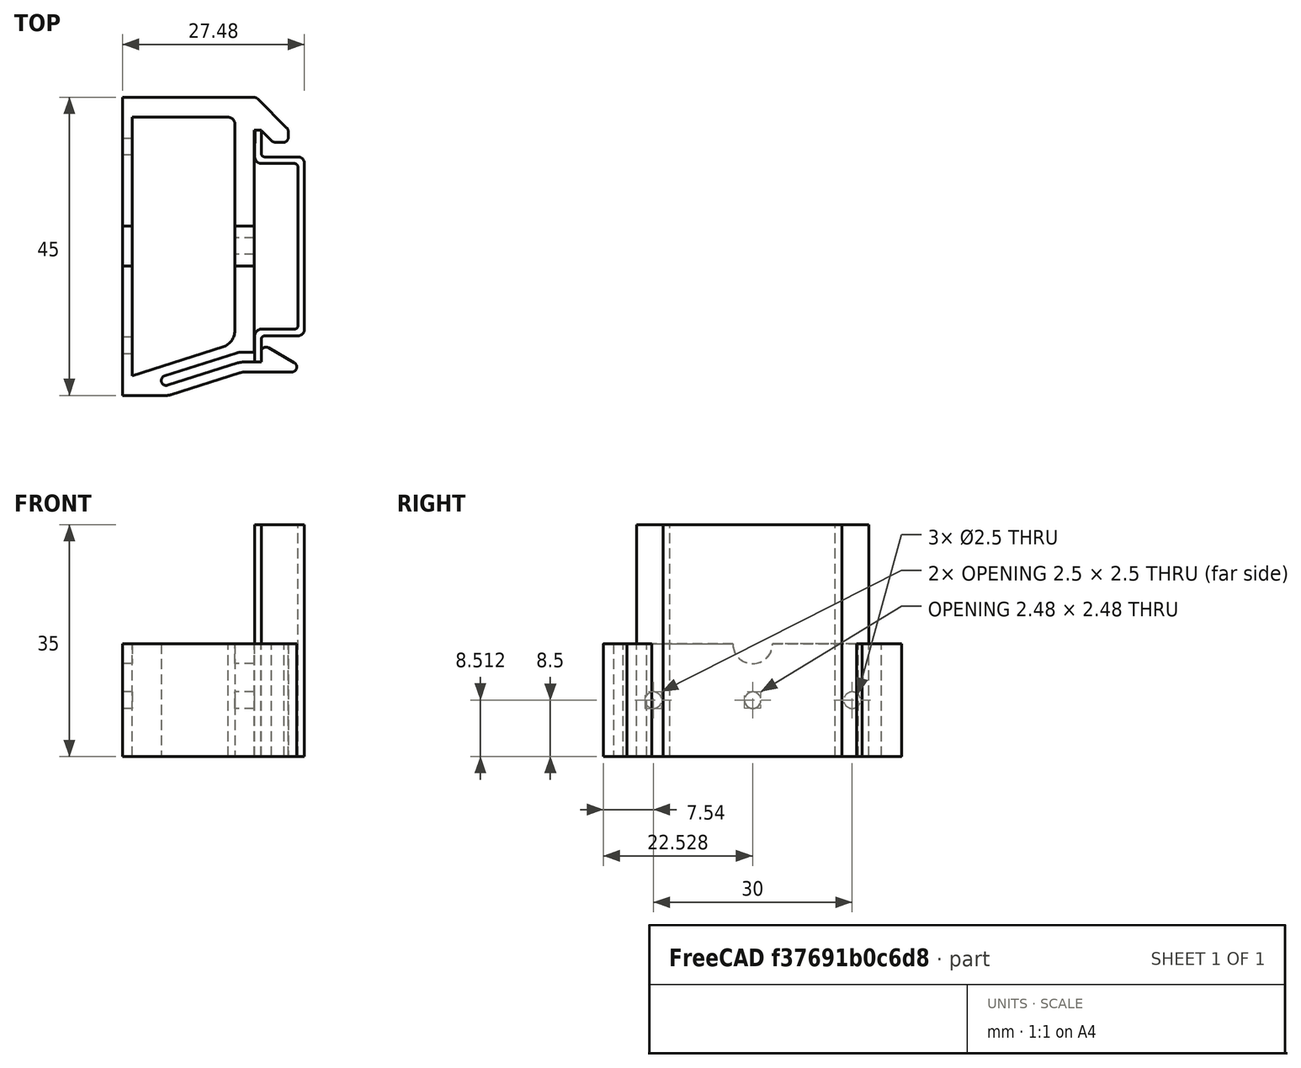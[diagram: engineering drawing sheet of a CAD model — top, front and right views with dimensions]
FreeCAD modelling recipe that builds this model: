
FCSTD DOCUMENT
Label: DIN_bracket_flat
License: CC-BY 3.0
LicenseURL: http://creativecommons.org/licenses/by/3.0/
objects: Part::Cylinder×4, Sketcher::SketchObject×2, PartDesign::Pad×2, Part::MultiFuse×1, Part::Cut×1
note: 12 computed .brp shape members not serialized (recipe doc carries the construction recipe); baked Part::Feature solids carry a one-line shape summary decoded from their .brp

FEATURE [Sketcher::SketchObject] Sketch
  Placement = pos=(-3,0,0) rot=(0,0,1;0rad)
  sketch-geometry (34):
    g0: LineSegment StartX=2.8168 StartY=22.4611 StartZ=0 EndX=-17 EndY=22.4611 EndZ=0
    g1: LineSegment StartX=-15.5 StartY=19.4611 StartZ=0 EndX=-1.04861 EndY=19.4611 EndZ=0
    g2: ArcOfCircle CenterX=-1.08879 CenterY=18.373 CenterZ=0 NormalX=0 NormalY=0 NormalZ=1 Radius=1.08879 StartAngle=6.28229 EndAngle=7.81708
    g3: LineSegment StartX=0 StartY=18.3721 StartZ=0 EndX=-0.0277889 EndY=-12.7677 EndZ=0
    g4: LineSegment StartX=1.58277 StartY=-19 StartZ=0 EndX=8.56539 EndY=-19 EndZ=0
    g5: ArcOfCircle CenterX=8.56539 CenterY=-18.25 CenterZ=0 NormalX=0 NormalY=0 NormalZ=1 Radius=0.75 StartAngle=4.71239 EndAngle=7.33038
    g6: LineSegment StartX=8.94039 StartY=-17.6005 StartZ=0 EndX=5.04328 EndY=-15.3505 EndZ=0
    g7: ArcOfCircle CenterX=4.66828 CenterY=-16 CenterZ=0 NormalX=0 NormalY=0 NormalZ=1 Radius=0.75 StartAngle=1.0472 EndAngle=3.14159
    g8: LineSegment StartX=3.91828 StartY=-17.5 StartZ=0 EndX=1.3506 EndY=-17.5 EndZ=0
    g9: LineSegment StartX=1.11842 StartY=-16 StartZ=0 EndX=2.91828 EndY=-16 EndZ=0
    g10: LineSegment StartX=2.91828 StartY=-16 StartZ=0 EndX=2.91828 EndY=17.5 EndZ=0
    g11: LineSegment StartX=2.91828 StartY=17.5 StartZ=0 EndX=3.91828 EndY=17.5 EndZ=0
    g12: LineSegment StartX=3.91828 StartY=17.5 StartZ=0 EndX=5.4708 EndY=15.9475 EndZ=0
    g13: ArcOfCircle CenterX=6.04763 CenterY=16.4268 CenterZ=0 NormalX=0 NormalY=0 NormalZ=1 Radius=0.75 StartAngle=3.83495 EndAngle=4.71239
    g14: LineSegment StartX=6.04763 StartY=15.6768 StartZ=0 EndX=7.42419 EndY=15.6768 EndZ=0
    g15: ArcOfCircle CenterX=7.28942 CenterY=16.4146 CenterZ=0 NormalX=0 NormalY=0 NormalZ=1 Radius=0.75 StartAngle=4.89306 EndAngle=6.44797
    g16: LineSegment StartX=8.02926 StartY=16.5376 StartZ=0 EndX=8.02926 EndY=17.321 EndZ=0
    g17: LineSegment StartX=3.91828 StartY=-16 StartZ=0 EndX=3.91828 EndY=-17.5 EndZ=0
    g18: LineSegment StartX=3.47066 StartY=22.1903 StartZ=0 EndX=7.80959 EndY=17.8513 EndZ=0
    g19: ArcOfCircle CenterX=7.27926 CenterY=17.321 CenterZ=0 NormalX=0 NormalY=0 NormalZ=1 Radius=0.75 StartAngle=0 EndAngle=0.785398
    g20: ArcOfCircle CenterX=2.8168 CenterY=21.5364 CenterZ=0 NormalX=0 NormalY=0 NormalZ=1 Radius=0.924699 StartAngle=0.785398 EndAngle=1.5708
    g21: LineSegment StartX=0.675806 StartY=-19.1404 StartZ=0 EndX=-9.7076 EndY=-22.4336 EndZ=0
    g22: LineSegment StartX=-15.5 StartY=-19.5498 StartZ=0 EndX=-1.81718 EndY=-15.2102 EndZ=0
    g23: LineSegment StartX=0.211458 StartY=-16.1404 StartZ=0 EndX=-10.6146 EndY=-19.574 EndZ=0
    g24: LineSegment StartX=-10.1611 StartY=-21.0038 StartZ=0 EndX=0.443632 EndY=-17.6404 EndZ=0
    g25: ArcOfCircle CenterX=-10.3878 CenterY=-20.2889 CenterZ=0 NormalX=0 NormalY=0 NormalZ=1 Radius=0.75 StartAngle=1.87794 EndAngle=5.0195
    g26: ArcOfCircle CenterX=-10.3878 CenterY=-20.2889 CenterZ=0 NormalX=0 NormalY=0 NormalZ=1 Radius=2.25 StartAngle=4.71239 EndAngle=5.01952
    g27: LineSegment StartX=-17 StartY=-22.5389 StartZ=0 EndX=-10.3878 EndY=-22.5389 EndZ=0
    g28: ArcOfCircle CenterX=-2.59257 CenterY=-12.7654 CenterZ=0 NormalX=0 NormalY=0 NormalZ=1 Radius=2.56478 StartAngle=5.01952 EndAngle=6.28229
    g29: ArcOfCircle CenterX=1.11842 CenterY=-19 CenterZ=0 NormalX=0 NormalY=0 NormalZ=1 Radius=3 StartAngle=1.5708 EndAngle=1.87792
    g30: ArcOfCircle CenterX=1.3506 CenterY=-20.5 CenterZ=0 NormalX=0 NormalY=0 NormalZ=1 Radius=3 StartAngle=1.5708 EndAngle=1.87792
    g31: ArcOfCircle CenterX=1.58277 CenterY=-22 CenterZ=0 NormalX=0 NormalY=0 NormalZ=1 Radius=3 StartAngle=1.5708 EndAngle=1.87792
    g32: LineSegment StartX=-15.5 StartY=-19.5498 StartZ=0 EndX=-15.5 EndY=19.4611 EndZ=0
    g33: LineSegment StartX=-17 StartY=22.4611 StartZ=0 EndX=-17 EndY=-22.5389 EndZ=0
  constraints (86):
    c: Coincident(g9,g10)
    c: Vertical(g10)
    c: Parallel(g8,g9)
    c: Vertical(g17)
    c: Coincident(g7,g17)
    c: Coincident(g7,g6)
    c: Tangent(g7,g17)
    c: Tangent(g7,g6)
    c: Coincident(g17,g8)
    c: Coincident(g2,g3)
    c: Coincident(g11,g10)
    c: Coincident(g6,g5)
    c: Coincident(g2,g1)
    c: DistanceY(g9,g8) = -1.5
    c: Distance(g8,g4) = 1.5
    c: Coincident(g4,g5)
    c: DistanceX(g22) = -15.5
    c: Tangent(g2,g3)
    c: DistanceX(g2) = 0
    c: Distance(g11) = 1
    c: Horizontal(g11)
    c: Coincident(g12,g11)
    c: Tangent(g13,g14)
    c: Horizontal(g0)
    c: Horizontal(g1)
    c: Angle(g6,g4) = 0.523599
    c: Radius(g5) = 0.75
    c: DistanceX(g9,g8) = 1
    c: Distance(g17) = 1.5
    c: Radius(g7) = 0.75
    c: Distance(g1,g0) = 3
    c: Vertical(g16)
    c: Coincident(g15,g16)
    c: Coincident(g14,g15)
    c: Horizontal(g14)
    c: Tangent(g5,g4)
    c: Coincident(g13,g12)
    c: Coincident(g13,g14)
    c: Tangent(g6,g5)
    c: Angle(g0,g18) = 2.35619
    c: Distance(g11,g18) = 3
    c: Parallel(g12,g18)
    c: Tangent(g16,g19)
    c: Tangent(g18,g19)
    c: Tangent(g0,g20)
    c: Tangent(g18,g20)
    c: Radius(g15) = 0.75
    c: Equal(g19,g15)
    c: Equal(g15,g13)
    c: Parallel(g22,g21)
    c: DistanceY(g8,g11) = 35
    c: Distance(g23,g22) = 1.5
    c: Distance(g24,g23) = 1.5
    c: Coincident(g25,g24)
    c: Tangent(g25,g24)
    c: Coincident(g25,g23)
    c: Tangent(g25,g23)
    c: Tangent(g27,g26)
    c: Tangent(g21,g26)
    c: Coincident(g26,g25)
    c: Parallel(g23,g24)
    c: Parallel(g8,g4)
    c: Horizontal(g4)
    c: DistanceY(g8) = -17.5
    c: Distance(g21,g24) = 1.5
    c: Parallel(g22,g23)
    c: Tangent(g3,g28)
    c: Tangent(g22,g28)
    c: Tangent(g9,g29)
    c: Tangent(g23,g29)
    c: Tangent(g8,g30)
    c: Tangent(g24,g30)
    c: Tangent(g4,g31)
    c: Tangent(g21,g31)
    c: Radius(g29) = 3
    c: Radius(g30) = 3
    c: Radius(g31) = 3
    c: Horizontal(g27)
    c: Coincident(g32,g1)
    c: Vertical(g32)
    c: Coincident(g33,g0)
    c: Parallel(g33,g32)
    c: DistanceX(g1,g0) = -1.5
    c: Coincident(g33,g27)
    c: Coincident(g32,g22)
    c: DistanceY(g27,g0) = 45
FEATURE [Sketcher::SketchObject] Sketch001
  Placement = pos=(0,17.5,0) rot=(0,0,1;0rad)
  sketch-geometry (20):
    g0: LineSegment StartX=0 StartY=0 StartZ=0 EndX=0.981065 EndY=0 EndZ=0
    g1: LineSegment StartX=0.981065 StartY=0 StartZ=0 EndX=0.981065 EndY=-3.53545 EndZ=0
    g2: ArcOfCircle CenterX=1.48107 CenterY=-3.53545 CenterZ=0 NormalX=0 NormalY=0 NormalZ=1 Radius=0.5 StartAngle=3.14159 EndAngle=4.71239
    g3: LineSegment StartX=1.48107 StartY=-4.03545 StartZ=0 EndX=6.48107 EndY=-4.03545 EndZ=0
    g4: ArcOfCircle CenterX=6.48107 CenterY=-5.03545 CenterZ=0 NormalX=0 NormalY=0 NormalZ=1 Radius=1 StartAngle=0 EndAngle=1.5708
    g5: LineSegment StartX=7.48107 StartY=-5.03545 StartZ=0 EndX=7.48107 EndY=-30.0354 EndZ=0
    g6: ArcOfCircle CenterX=6.48107 CenterY=-30.0354 CenterZ=0 NormalX=0 NormalY=0 NormalZ=1 Radius=1 StartAngle=4.71239 EndAngle=6.28319
    g7: LineSegment StartX=6.48107 StartY=-31.0354 StartZ=0 EndX=1.48107 EndY=-31.0354 EndZ=0
    g8: ArcOfCircle CenterX=1.48107 CenterY=-31.5354 CenterZ=0 NormalX=0 NormalY=0 NormalZ=1 Radius=0.5 StartAngle=1.5708 EndAngle=3.14159
    g9: LineSegment StartX=0.981065 StartY=-31.5354 StartZ=0 EndX=0.981065 EndY=-35 EndZ=0
    g10: LineSegment StartX=0.981065 StartY=-35 StartZ=0 EndX=-0.018935 EndY=-35 EndZ=0
    g11: LineSegment StartX=-0.018935 StartY=-35 StartZ=0 EndX=-0.018935 EndY=-31.0354 EndZ=0
    g12: ArcOfCircle CenterX=0.981065 CenterY=-31.0354 CenterZ=0 NormalX=0 NormalY=0 NormalZ=1 Radius=1 StartAngle=1.5708 EndAngle=3.14159
    g13: LineSegment StartX=0.981065 StartY=-30.0354 StartZ=0 EndX=5.98107 EndY=-30.0354 EndZ=0
    g14: ArcOfCircle CenterX=5.98107 CenterY=-29.5354 CenterZ=0 NormalX=0 NormalY=0 NormalZ=1 Radius=0.5 StartAngle=4.71239 EndAngle=6.28319
    g15: LineSegment StartX=6.48107 StartY=-29.5354 StartZ=0 EndX=6.48107 EndY=-5.53545 EndZ=0
    g16: ArcOfCircle CenterX=5.98107 CenterY=-5.53545 CenterZ=0 NormalX=0 NormalY=0 NormalZ=1 Radius=0.5 StartAngle=0 EndAngle=1.5708
    g17: LineSegment StartX=5.98107 StartY=-5.03545 StartZ=0 EndX=0.981065 EndY=-5.03545 EndZ=0
    g18: ArcOfCircle CenterX=0.981065 CenterY=-4.03545 CenterZ=0 NormalX=0 NormalY=0 NormalZ=1 Radius=1 StartAngle=3.14159 EndAngle=4.71239
    g19: LineSegment StartX=-0.018935 StartY=-4.03545 StartZ=0 EndX=0 EndY=0 EndZ=0
  constraints (9):
    c: DistanceY(g-1,g10) = -35
    c: DistanceX(g0) = 0
    c: DistanceY(g0) = 0
    c: Horizontal(g0)
    c: Coincident(g19,g-1)
    c: Coincident(g1,g0)
    c: Horizontal(g10)
    c: Coincident(g9,g10)
    c: Coincident(g11,g10)
FEATURE [PartDesign::Pad] Pad001  label="DIN rail"
  Length = 35
  Length2 = 100
  Placement = pos=(0,17.5,0) rot=(0,0,1;0rad)
  Sketch = -> Sketch001
  Type = 0
FEATURE [PartDesign::Pad] Pad  label="DIN bracket solid"
  Length = 17
  Length2 = 100
  Placement = pos=(-3,0,0) rot=(0,0,1;0rad)
  Sketch = -> Sketch
  Type = 0
FEATURE [Part::Cylinder] Cylinder  label="bracket hole"
  Angle = 360
  Height = 10
  Placement = pos=(5,0,8.5) rot=(0,-1,0;1.5708rad)
  Radius = 1.25
FEATURE [Part::Cylinder] Cylinder001  label="bracket hole001"
  Angle = 360
  Height = 10
  Placement = pos=(-15,15,8.5) rot=(0,-1,0;1.5708rad)
  Radius = 1.25
FEATURE [Part::Cylinder] Cylinder002  label="bracket hole002"
  Angle = 360
  Height = 10
  Placement = pos=(-15,-15,8.5) rot=(0,-1,0;1.5708rad)
  Radius = 1.25
FEATURE [Part::Cylinder] Cylinder003  label="bracket hole003"
  Angle = 360
  Height = 25
  Placement = pos=(0,0,17) rot=(0,-1,0;1.5708rad)
  Radius = 3
FEATURE [Part::MultiFuse] Fusion  label="cuts"
  Shapes = -> [Cylinder003,Cylinder,Cylinder002,Cylinder001]
FEATURE [Part::Cut] Cut  label="bracket"
  Base = -> Pad
  Tool = -> Fusion
